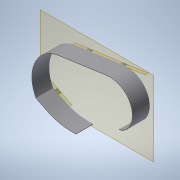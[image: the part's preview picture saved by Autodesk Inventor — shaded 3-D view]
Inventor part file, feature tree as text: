
AUTODESK INVENTOR PART (.ipt)
format: ipt  version: 2021 (Build 250183000, 183)  size: 177,664 bytes
history: native  units: in
note: dims shown in document units (in); Inventor stores cm internally (conversion verified against a paired STEP export)
features: reference x14, plane x3, extrude x3, sketch x3, other x3
ambient origin geometry x8: Origin, YZ Plane, XZ Plane, XY Plane, X Axis, Y Axis, Z Axis, Center Point
bodies: Solid1 (feature_tree)
feature tree (26):
  plane  "Work Plane1"
  extrude  "Extrusion1"  Depth=0.75in
  plane  "Work Plane2"
  extrude  "Extrusion2"  Depth=5.35in
  plane  "Work Plane5"
  extrude  "Extrusion5"  Depth=0.1024in TaperAngle=0.0deg
  sketch  "Sketch1"  dims[d3=3.0in d4=0.0in d7=0.75in]
  reference  "Reference2"
  reference  "Reference3"
  reference  "Reference4"
  reference  "Reference5"
  reference  "Reference6"
  reference  "Reference7"
  reference  "Reference8"
  sketch  "Sketch2"  dims[d8=2.65in d9=5.35in]
  reference  "Reference9"
  reference  "Reference10"
  reference  "Reference11"
  reference  "Reference16"
  sketch  "Sketch5"  dims[d10=0.75in d11=0.1024in d12=0.0in d24=0.1024in d25=0.395in d26=0.395in d27=0.1024in d28=0.0in]
  reference  "Reference17"
  reference  "Reference18"
  reference  "Reference19"
  other  "ChainGuardAssembly.iam"
  other  "DiffMountRightipt:1"
  other  "Assembly1"
